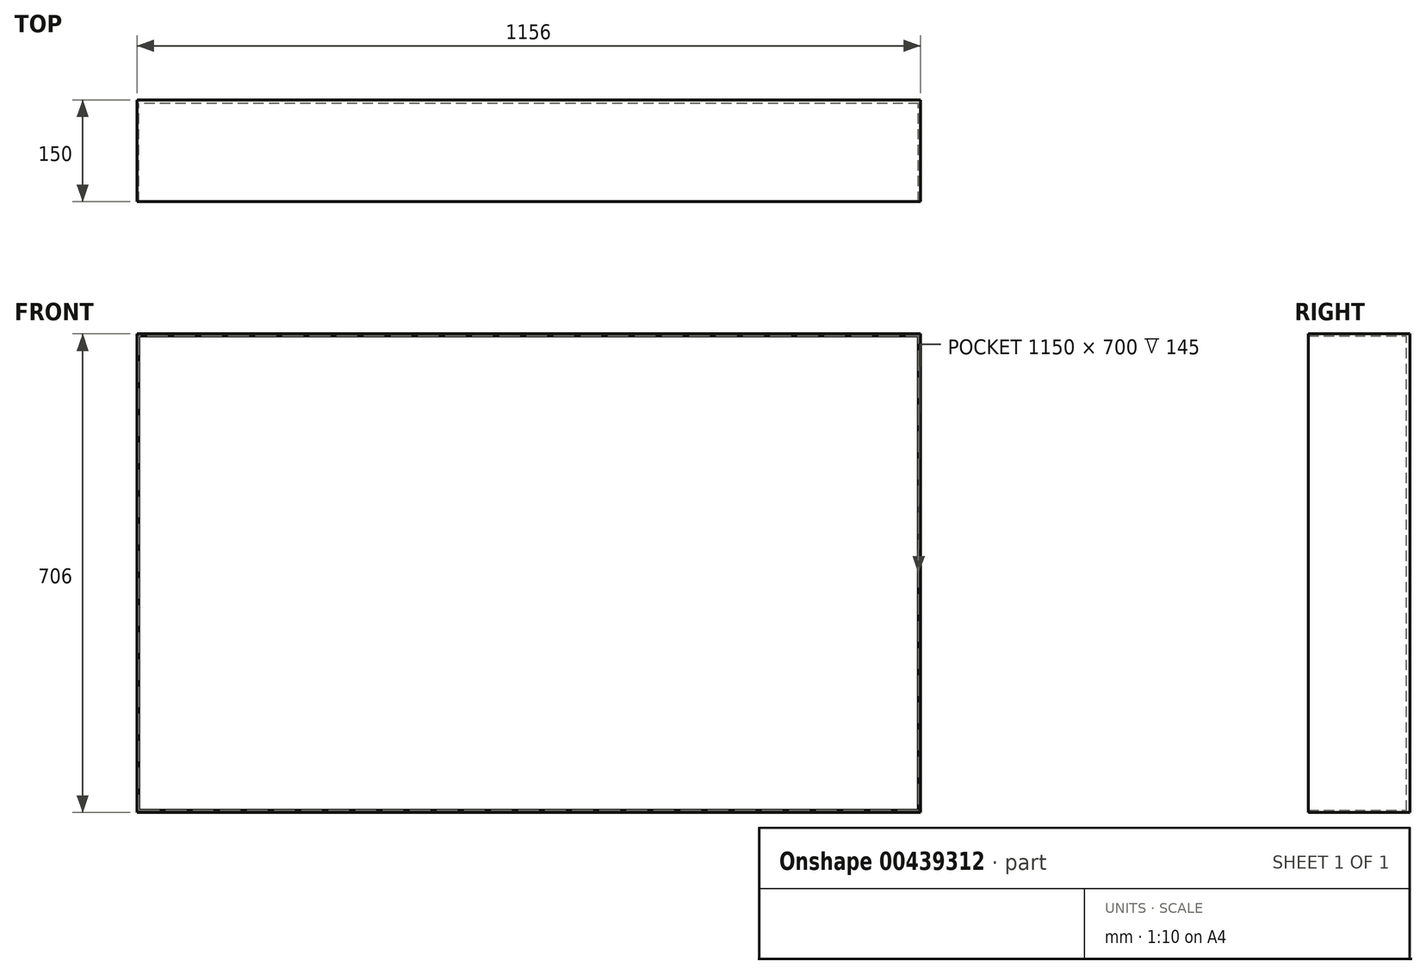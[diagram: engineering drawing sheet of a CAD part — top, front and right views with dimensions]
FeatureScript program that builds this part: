
annotation { "Feature Type Name" : "Feature", "Feature Type Description" : "" }
export const myFeature = defineFeature(function(context is Context, id is Id, definition is map)
    precondition{}
    {
        {
            var Q0;
            Q0=qCreatedBy(makeId("Front.planeOp"),FACE);
            var sketch = newSketch(context, id + "F0", { "sketchPlane" : qUnion([Q0])});
            skLineSegment(sketch, "E0.bottom", {"start": v(-71.24, 38.34) * mm, "end": v(1078.76, 38.34) * mm});
            skLineSegment(sketch, "E0.top", {"start": v(-71.24, -661.66) * mm, "end": v(1078.76, -661.66) * mm});
            skLineSegment(sketch, "E0.left", {"start": v(-71.24, 38.34) * mm, "end": v(-71.24, -661.66) * mm});
            skLineSegment(sketch, "E0.right", {"start": v(1078.76, 38.34) * mm, "end": v(1078.76, -661.66) * mm});
            skLineSegment(sketch, "E1.0", {"start": v(-74.24, 41.34) * mm, "end": v(1081.76, 41.34) * mm});
            skLineSegment(sketch, "E1.1", {"start": v(-74.24, 41.34) * mm, "end": v(-74.24, -664.66) * mm});
            skLineSegment(sketch, "E1.2", {"start": v(-74.24, -664.66) * mm, "end": v(1081.76, -664.66) * mm});
            skLineSegment(sketch, "E1.3", {"start": v(1081.76, 41.34) * mm, "end": v(1081.76, -664.66) * mm});
            skSolve(sketch);
        }
        {
            var Q0;
            Q0 = qSketchRegion(id + "F0", true);
            extrude(context, id + "F1", {"entities" : qUnion([Q0]), "depth" : 150 * mm});
        }
        {
            var Q0;
            Q0=makeQuery(id+"F1.opExtrude","SWEPT_FACE",FACE,{"disambiguationData":[OSD([sQuery(id+"F0.wireOp",EDGE,"E1.1")])]});
            var sketch = newSketch(context, id + "F2", { "sketchPlane" : qUnion([Q0])});
            skLineSegment(sketch, "E2.bottom", {"start": v(0, 41.34) * mm, "end": v(5, 41.34) * mm});
            skLineSegment(sketch, "E2.top", {"start": v(0, -664.66) * mm, "end": v(5, -664.66) * mm});
            skLineSegment(sketch, "E2.left", {"start": v(0, 41.34) * mm, "end": v(0, -664.66) * mm});
            skLineSegment(sketch, "E2.right", {"start": v(5, 41.34) * mm, "end": v(5, -664.66) * mm});
            skSolve(sketch);
        }
        {
            var Q0;
            Q0 = qSketchRegion(id + "F2", true);
            var Q1;
            Q1=makeQuery(id+"F1.opExtrude","SWEPT_FACE",FACE,{"disambiguationData":[OSD([sQuery(id+"F0.wireOp",EDGE,"E0.right")])]});
            extrude(context, id + "F3", {"entities" : qUnion([Q0]), "operationType" : NewBodyOperationType.ADD, "endBound" : BoundingType.UP_TO_SURFACE, "oppositeDirection" : true, "endBoundEntityFace" : qUnion([Q1]), "depth" : 122.6 * mm});
        }
    });
